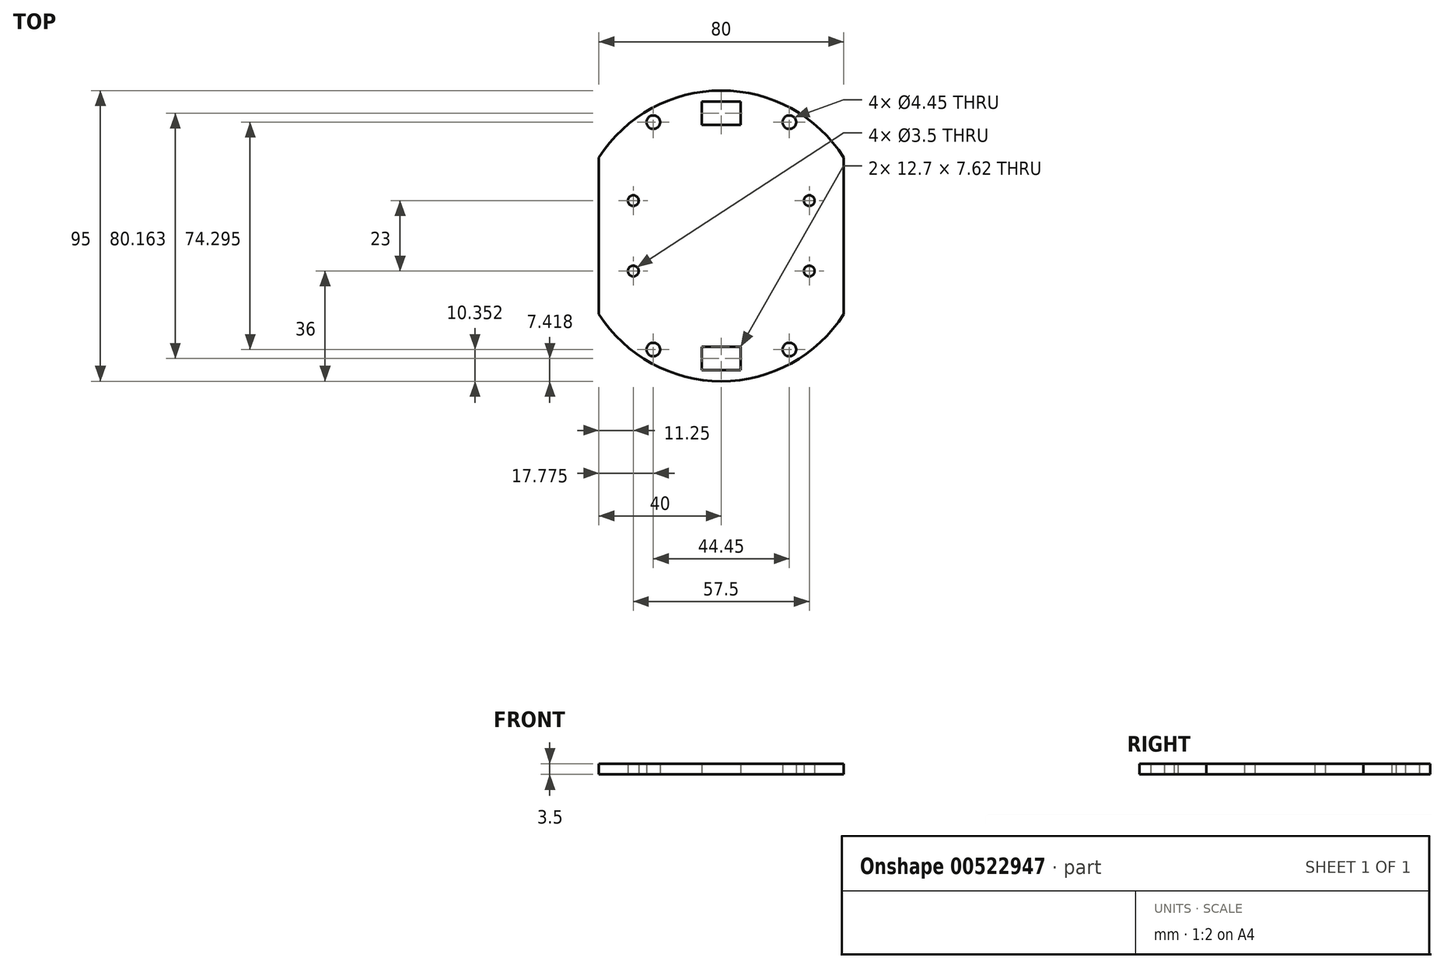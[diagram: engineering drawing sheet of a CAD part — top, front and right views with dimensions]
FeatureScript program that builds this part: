
annotation { "Feature Type Name" : "Feature", "Feature Type Description" : "" }
export const myFeature = defineFeature(function(context is Context, id is Id, definition is map)
    precondition{}
    {
        {
            var Q0;
            Q0=qCreatedBy(makeId("Top.planeOp"),FACE);
            var sketch = newSketch(context, id + "F0", { "sketchPlane" : qUnion([Q0])});
            skCircle(sketch, "E0", {"center": v(0, 0) * mm, "radius": 47.5 * mm});
            skCircle(sketch, "E1", {"center": v(22.23, -37.15) * mm, "radius": 2.22 * mm});
            skLineSegment(sketch, "E2", {"start": v(40, 25.62) * mm, "end": v(40, -25.62) * mm});
            skLineSegment(sketch, "E3.bottom", {"start": v(-6.35, 43.9) * mm, "end": v(6.35, 43.9) * mm});
            skLineSegment(sketch, "E3.top", {"start": v(-6.35, 36.27) * mm, "end": v(6.35, 36.27) * mm});
            skLineSegment(sketch, "E3.left", {"start": v(-6.35, 43.9) * mm, "end": v(-6.35, 36.27) * mm});
            skLineSegment(sketch, "E3.right", {"start": v(6.35, 43.9) * mm, "end": v(6.35, 36.27) * mm});
            skLineSegment(sketch, "E4.MirrorCS", {"start": v(-40, 25.62) * mm, "end": v(-40, -25.62) * mm});
            skLineSegment(sketch, "E5.MirrorCS", {"start": v(6.35, -43.9) * mm, "end": v(6.35, -36.27) * mm});
            skLineSegment(sketch, "E6.MirrorCS", {"start": v(-6.35, -43.9) * mm, "end": v(-6.35, -36.27) * mm});
            skLineSegment(sketch, "E7.MirrorCS", {"start": v(-6.35, -36.27) * mm, "end": v(6.35, -36.27) * mm});
            skLineSegment(sketch, "E8.MirrorCS", {"start": v(-6.35, -43.9) * mm, "end": v(6.35, -43.9) * mm});
            skCircle(sketch, "E9.MirrorC", {"center": v(-22.23, -37.15) * mm, "radius": 2.22 * mm});
            skCircle(sketch, "E10.MirrorC", {"center": v(-22.23, 37.15) * mm, "radius": 2.22 * mm});
            skCircle(sketch, "E11.MirrorC", {"center": v(22.23, 37.15) * mm, "radius": 2.22 * mm});
            skCircle(sketch, "E12", {"center": v(28.75, -11.5) * mm, "radius": 1.75 * mm});
            skCircle(sketch, "E13.MirrorC", {"center": v(-28.75, -11.5) * mm, "radius": 1.75 * mm});
            skCircle(sketch, "E14.MirrorC", {"center": v(28.75, 11.5) * mm, "radius": 1.75 * mm});
            skCircle(sketch, "E15.MirrorC", {"center": v(-28.75, 11.5) * mm, "radius": 1.75 * mm});
            skSolve(sketch);
        }
        {
            var Q0;
            Q0=makeQuery(id+"F0.imprint","IMPRINT",FACE,{"disambiguationData":[TD([[makeQuery(id+"F0.imprint","IMPRINT",EDGE,{"derivedFrom":sQuery(id+"F0.wireOp",EDGE,"E1")}),-1.0]])]});
            extrude(context, id + "F1", {"entities" : qUnion([Q0]), "depth" : 3.5 * mm, "offsetDistance" : 25.4 * mm});
        }
    });
